# Revit family: Haworth_Planes_HeightAdjustBench_120
name_source: partatom
category: Furniture Systems
revit_build: Autodesk Revit 2018 (Build: 20170223_1515(x64)
units: mm (PartAtom-declared; Revit-internal decimal feet)

## family parameters
Always vertical = Yes
Cut with Voids When Loaded = No
OmniClass Number = 23.40.70.14.64.21
OmniClass Title = Systems Furniture
Part Type = Normal
Room Calculation Point = No
Round Connector Dimension = Use Diameter
Shared = No
Work Plane-Based = No

## types (4) — shared parameters
Actual Height = 40"
Assembly Code = E2020200
Base Tube Finish = Haworth _ Paint _ Black
Box Body Finish = Haworth _ Paint _ Black
Crank Offset = 13 1/8"
Custom Size = No
Gap Depth = 1 13/16"
Height = 40"
J-Rail Height = 22 5/8"
Leg Height = 38 13/16"
Leg Offset = 10 5/32"
Lever Depth = 12"
Manufacturer = Haworth
Max. Depth = 30"
Max. Height = 46"
Max. Overall Depth = 63"
Max. Width = 58"
Min. Depth = 23"
Min. Height = 27"
Min. Overall Depth = 51"
Min. Width = 46"
Model = TACZ
Revision Number = 1
Size = Verify Final Dim. w/ Haworth
Standard Overall Depth = 51, 63 in.
Standard Width = 46, 52, 58 in.
Standard Worksurface Depth = 23, 24, 29, 30 in.
Table Thickness = 1 3/16"
Touch Pad Width = 2 3/4"
Trim Finish = Haworth _ Paint _ Metallic Champagne
URL = www.haworth.com
URL - Product = https://www.haworth.com
Warranty = https://www.haworth.com
Worksurface Distance = 3 5/8"

## per-type parameters (varying)
| type | Actual Depth | Actual Overall Depth | Actual Width | Depth | Description | Electric Adjustment | Hand Crank | J-Rail Width | Leg Side Offset | Width |
| 58w 30d - Electric Adjustment | 30" | 63 5/8" | 58" | 30" | Haworth - Planes HAT - 120 Bench - 58w 30d - Electric Adjustment | Yes | No | 43 3/4" | 43 3/4" | 58" |
| 58w 30d - Crank Adjustment | 30" | 63 5/8" | 58" | 30" | Haworth - Planes HAT - 120 Bench - 58w 30d - Crank Adjustment | No | Yes | 43 3/4" | 43 3/4" | 58" |
| 46w 23d - Crank Adjustment | 23" | 49 5/8" | 46" | 23" | Haworth - Planes HAT - 120 Bench - 46w 23d - Crank Adjustment | No | Yes | 33 3/4" | 33 3/4" | 46" |
| 52w 24d - Electric Adjustment | 24" | 51 5/8" | 52" | 24" | Haworth - Planes HAT - 120 Bench - 52w 24d - Electric Adjustment | Yes | No | 38 3/4" | 38 3/4" | 52" |

## geometry (parser evidence)
native form markers: Sweep x14
no freeform markers — native parametric forms only
